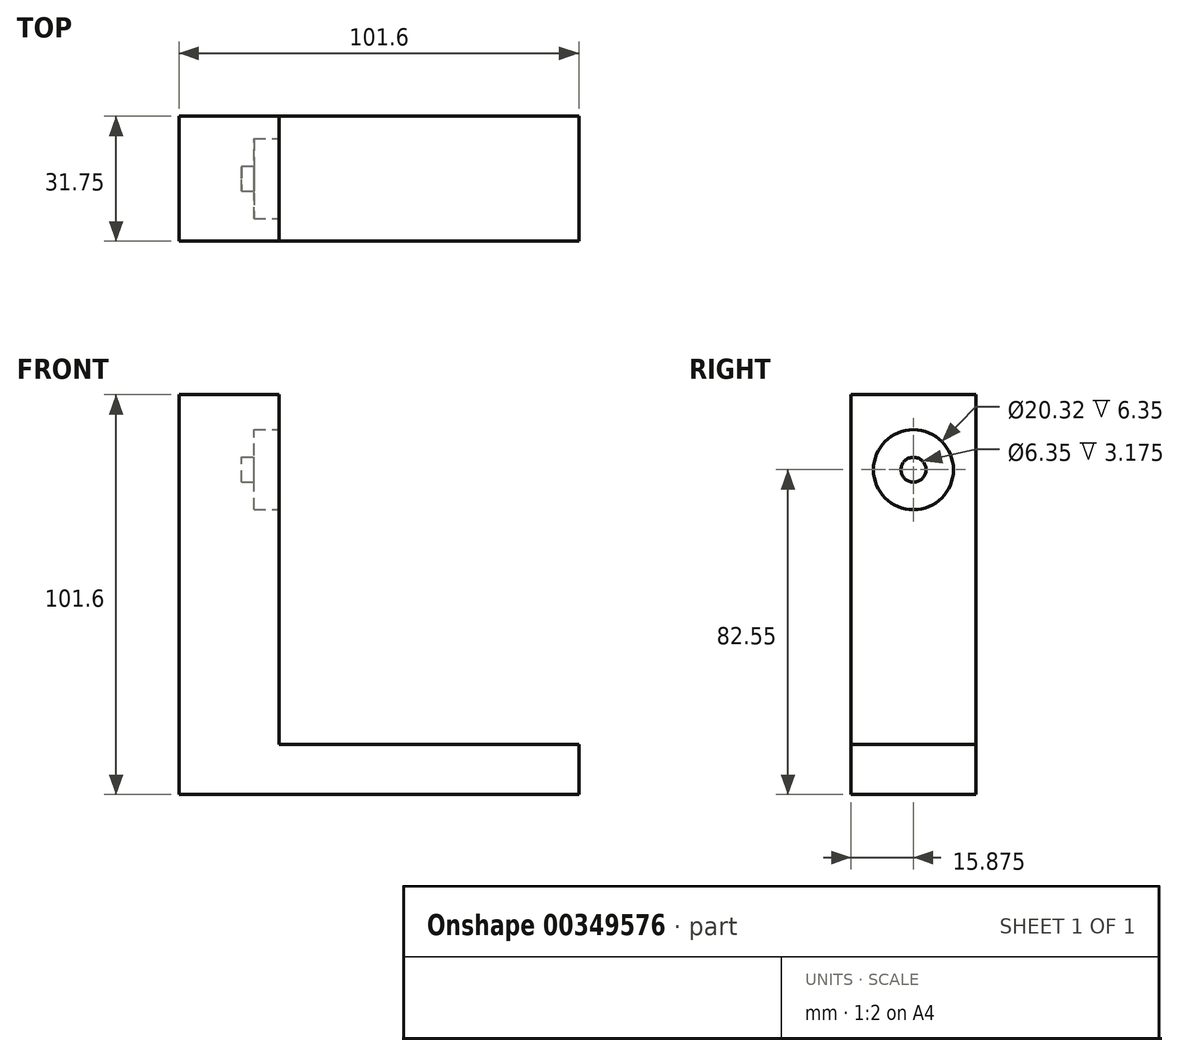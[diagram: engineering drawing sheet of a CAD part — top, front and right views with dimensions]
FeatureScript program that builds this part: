
annotation { "Feature Type Name" : "Feature", "Feature Type Description" : "" }
export const myFeature = defineFeature(function(context is Context, id is Id, definition is map)
    precondition{}
    {
        {
            var Q0;
            Q0=qCreatedBy(makeId("Right.planeOp"),FACE);
            var sketch = newSketch(context, id + "F0", { "sketchPlane" : qUnion([Q0])});
            skLineSegment(sketch, "E0.bottom", {"start": v(0, 0) * mm, "end": v(31.75, 0) * mm});
            skLineSegment(sketch, "E0.top", {"start": v(0, 101.6) * mm, "end": v(31.75, 101.6) * mm});
            skLineSegment(sketch, "E0.left", {"start": v(0, 0) * mm, "end": v(0, 101.6) * mm});
            skLineSegment(sketch, "E0.right", {"start": v(31.75, 0) * mm, "end": v(31.75, 101.6) * mm});
            skSolve(sketch);
        }
        {
            var Q0;
            Q0 = qSketchRegion(id + "F0", true);
            extrude(context, id + "F1", {"entities" : qUnion([Q0]), "oppositeDirection" : true, "depth" : 25.4 * mm});
        }
        {
            var Q0;
            Q0=makeQuery(id+"F1.opExtrude","CAP_FACE",FACE,{"disambiguationData":[OSD([sQuery(id+"F0.wireOp",EDGE,"E0.bottom"),sQuery(id+"F0.wireOp",EDGE,"E0.top"),sQuery(id+"F0.wireOp",EDGE,"E0.left"),sQuery(id+"F0.wireOp",EDGE,"E0.right")])],"isStart":true});
            var sketch = newSketch(context, id + "F2", { "sketchPlane" : qUnion([Q0])});
            skCircle(sketch, "E1", {"center": v(15.88, 82.55) * mm, "radius": 10.16 * mm});
            skSolve(sketch);
        }
        {
            var Q0;
            Q0 = qSketchRegion(id + "F2", true);
            extrude(context, id + "F3", {"entities" : qUnion([Q0]), "operationType" : NewBodyOperationType.REMOVE, "oppositeDirection" : true, "depth" : 6.35 * mm});
        }
        {
            var Q0;
            Q0=makeQuery(id+"F3.boolean.opBoolean","COPY",FACE,{"derivedFrom":makeQuery(id+"F3.opExtrude","CAP_FACE",FACE,{"disambiguationData":[OSD([sQuery(id+"F2.wireOp",EDGE,"E1")])],"isStart":false})});
            var sketch = newSketch(context, id + "F4", { "sketchPlane" : qUnion([Q0])});
            skCircle(sketch, "E2", {"center": v(15.88, 82.55) * mm, "radius": 3.18 * mm});
            skSolve(sketch);
        }
        {
            var Q0;
            Q0 = qSketchRegion(id + "F4", true);
            extrude(context, id + "F5", {"entities" : qUnion([Q0]), "operationType" : NewBodyOperationType.REMOVE, "oppositeDirection" : true, "depth" : 3.17 * mm});
        }
        {
            var Q0;
            Q0=makeQuery(id+"F1.opExtrude","SWEPT_FACE",FACE,{"disambiguationData":[OSD([sQuery(id+"F0.wireOp",EDGE,"E0.left")])]});
            var sketch = newSketch(context, id + "F6", { "sketchPlane" : qUnion([Q0])});
            skLineSegment(sketch, "E3.bottom", {"start": v(0, 0) * mm, "end": v(76.2, 0) * mm});
            skLineSegment(sketch, "E3.top", {"start": v(0, 12.7) * mm, "end": v(76.2, 12.7) * mm});
            skLineSegment(sketch, "E3.left", {"start": v(0, 0) * mm, "end": v(0, 12.7) * mm});
            skLineSegment(sketch, "E3.right", {"start": v(76.2, 0) * mm, "end": v(76.2, 12.7) * mm});
            skSolve(sketch);
        }
        {
            var Q0;
            Q0 = qSketchRegion(id + "F6", true);
            extrude(context, id + "F7", {"entities" : qUnion([Q0]), "operationType" : NewBodyOperationType.ADD, "oppositeDirection" : true, "depth" : 31.75 * mm});
        }
    });
